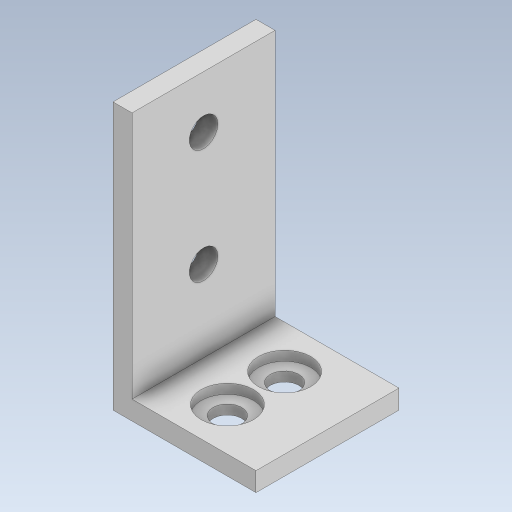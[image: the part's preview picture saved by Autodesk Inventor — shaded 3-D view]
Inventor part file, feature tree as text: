
AUTODESK INVENTOR PART (.ipt)
format: ipt  version: 2023.5 (Build 275446000, 446)  size: 312,832 bytes
history: native  units: in
note: dims shown in document units (in); Inventor stores cm internally (conversion verified against a paired STEP export)
features: extrude x4, sketch x2
ambient origin geometry x8: Origin, YZ Plane, XZ Plane, XY Plane, X Axis, Y Axis, Z Axis, Center Point
bodies: Solid1 (feature_tree)
feature tree (6):
  sketch  "Sketch1"  dims[d0=0.5906in d1=0.5906in]
  extrude  "Extrusion1"  Depth=0.5906in
  extrude  "Extrusion2"  Depth=0.1181in
  extrude  "Extrusion3"  Depth=0.0787in
  extrude  "Extrusion4"  Depth=0.0787in
  sketch  "Sketch2"  dims[d2=0.0787in d3=0.1181in d4=0.2165in d5=0.1772in d6=0.0787in d7=0.0in d8=0.0394in d9=0.0in d10=1.1024in d11=0.0in d12=0.1181in d13=0.3346in d14=0.1181in d15=0.8071in d16=0.0787in d17=0.0in]
